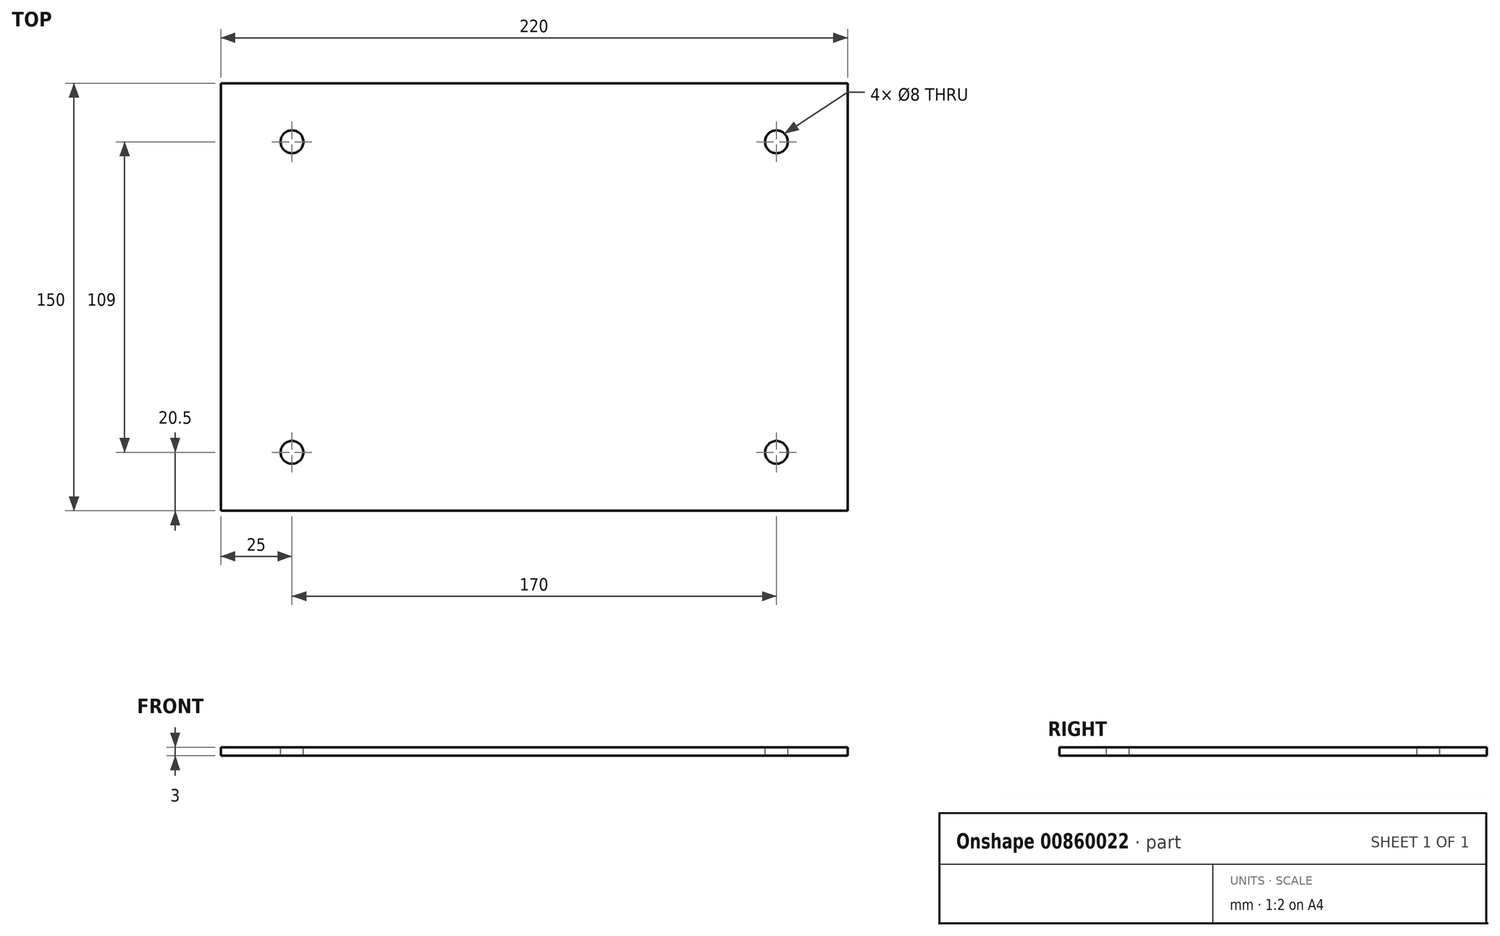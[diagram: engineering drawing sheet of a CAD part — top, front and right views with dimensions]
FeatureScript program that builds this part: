
annotation { "Feature Type Name" : "Feature", "Feature Type Description" : "" }
export const myFeature = defineFeature(function(context is Context, id is Id, definition is map)
    precondition{}
    {
        {
            var Q0;
            Q0=qCreatedBy(makeId("Top.planeOp"),FACE);
            var sketch = newSketch(context, id + "F0", { "sketchPlane" : qUnion([Q0])});
            skLineSegment(sketch, "E0.bottom", {"start": v(110, 75) * mm, "end": v(-110, 75) * mm});
            skLineSegment(sketch, "E0.top", {"start": v(110, -75) * mm, "end": v(-110, -75) * mm});
            skLineSegment(sketch, "E0.left", {"start": v(110, 75) * mm, "end": v(110, -75) * mm});
            skLineSegment(sketch, "E0.right", {"start": v(-110, 75) * mm, "end": v(-110, -75) * mm});
            skPoint(sketch, "E0.middle", {"position": v(0, 0) * mm});
            skSolve(sketch);
        }
        {
            var Q0;
            Q0=makeQuery(id+"F0.imprint","IMPRINT",FACE,{"disambiguationData":[TD([[makeQuery(id+"F0.imprint","IMPRINT",EDGE,{"derivedFrom":sQuery(id+"F0.wireOp",EDGE,"E0.bottom")}),1.0]])]});
            var sketch = newSketch(context, id + "F1", { "sketchPlane" : qUnion([Q0])});
            skLineSegment(sketch, "E1.bottom", {"start": v(85, 54.5) * mm, "end": v(-85, 54.5) * mm, "construction": true});
            skLineSegment(sketch, "E1.top", {"start": v(85, -54.5) * mm, "end": v(-85, -54.5) * mm, "construction": true});
            skLineSegment(sketch, "E1.left", {"start": v(85, 54.5) * mm, "end": v(85, -54.5) * mm, "construction": true});
            skLineSegment(sketch, "E1.right", {"start": v(-85, 54.5) * mm, "end": v(-85, -54.5) * mm, "construction": true});
            skPoint(sketch, "E1.middle", {"position": v(0, 0) * mm});
            skSolve(sketch);
        }
        {
            var Q0;
            Q0 = qSketchRegion(id + "F0", true);
            extrude(context, id + "F2", {"entities" : qUnion([Q0]), "oppositeDirection" : true, "depth" : 3 * mm, "offsetDistance" : 25 * mm});
        }
        {
            var Q0;
            Q0=sQuery(id+"F1.wireOp",VERTEX,"E1.top.start");
            var Q1;
            Q1=sQuery(id+"F1.wireOp",VERTEX,"E1.bottom.start");
            var Q2;
            Q2=sQuery(id+"F1.wireOp",VERTEX,"E1.bottom.end");
            var Q3;
            Q3=sQuery(id+"F1.wireOp",VERTEX,"E1.top.end");
            var Q4;
            Q4=makeQuery(id+"F2.opExtrude","SWEPT_BODY",BODY,{"disambiguationData":[OSD([sQuery(id+"F0.wireOp",EDGE,"E0.bottom"),sQuery(id+"F0.wireOp",EDGE,"E0.top"),sQuery(id+"F0.wireOp",EDGE,"E0.left"),sQuery(id+"F0.wireOp",EDGE,"E0.right")])]});
            hole(context, id + "F3", {"style" : HoleStyle.SIMPLE, "endStyle" : HoleEndStyle.THROUGH, "holeDiameter" : 8 * mm, "majorDiameter" : 5 * mm, "isTappedThrough" : true, "tappedDepth" : 12 * mm, "tapClearance" : 3, "locations" : qUnion([Q0, Q1, Q2, Q3]), "scope" : qUnion([Q4])});
        }
    });
